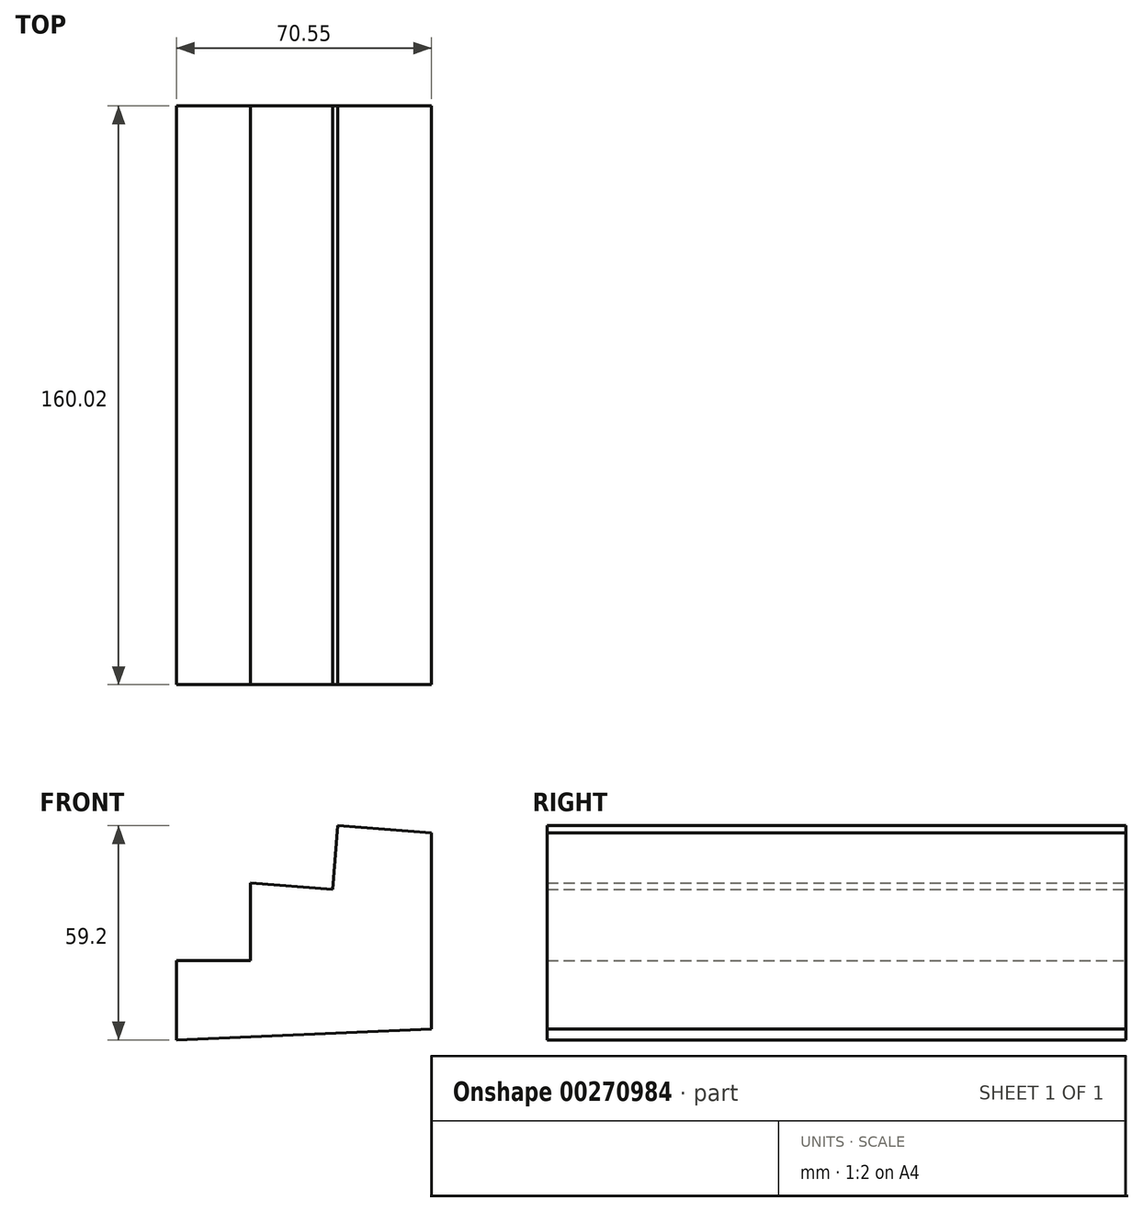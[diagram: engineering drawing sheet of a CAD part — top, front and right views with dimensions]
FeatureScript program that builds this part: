
annotation { "Feature Type Name" : "Feature", "Feature Type Description" : "" }
export const myFeature = defineFeature(function(context is Context, id is Id, definition is map)
    precondition{}
    {
        {
            var Q0;
            Q0=qCreatedBy(makeId("Front.planeOp"),FACE);
            var sketch = newSketch(context, id + "F0", { "sketchPlane" : qUnion([Q0])});
            skLineSegment(sketch, "E0", {"start": v(-43.25, -59.2) * mm, "end": v(-43.25, -37.24) * mm});
            skLineSegment(sketch, "E1", {"start": v(-43.25, -37.24) * mm, "end": v(-22.82, -37.24) * mm});
            skLineSegment(sketch, "E2", {"start": v(-22.82, -37.24) * mm, "end": v(-22.82, -15.85) * mm});
            skLineSegment(sketch, "E3", {"start": v(-22.82, -15.85) * mm, "end": v(0, -17.57) * mm});
            skLineSegment(sketch, "E4", {"start": v(0, -17.57) * mm, "end": v(1.32, 0) * mm});
            skLineSegment(sketch, "E5", {"start": v(1.32, 0) * mm, "end": v(27.3, -1.96) * mm});
            skLineSegment(sketch, "E6", {"start": v(27.3, -1.96) * mm, "end": v(27.3, -56.14) * mm});
            skLineSegment(sketch, "E7", {"start": v(27.3, -56.14) * mm, "end": v(-43.25, -59.2) * mm});
            skSolve(sketch);
        }
        {
            var Q0;
            Q0 = qSketchRegion(id + "F0", true);
            extrude(context, id + "F1", {"entities" : qUnion([Q0]), "depth" : 160.02 * mm});
        }
    });
